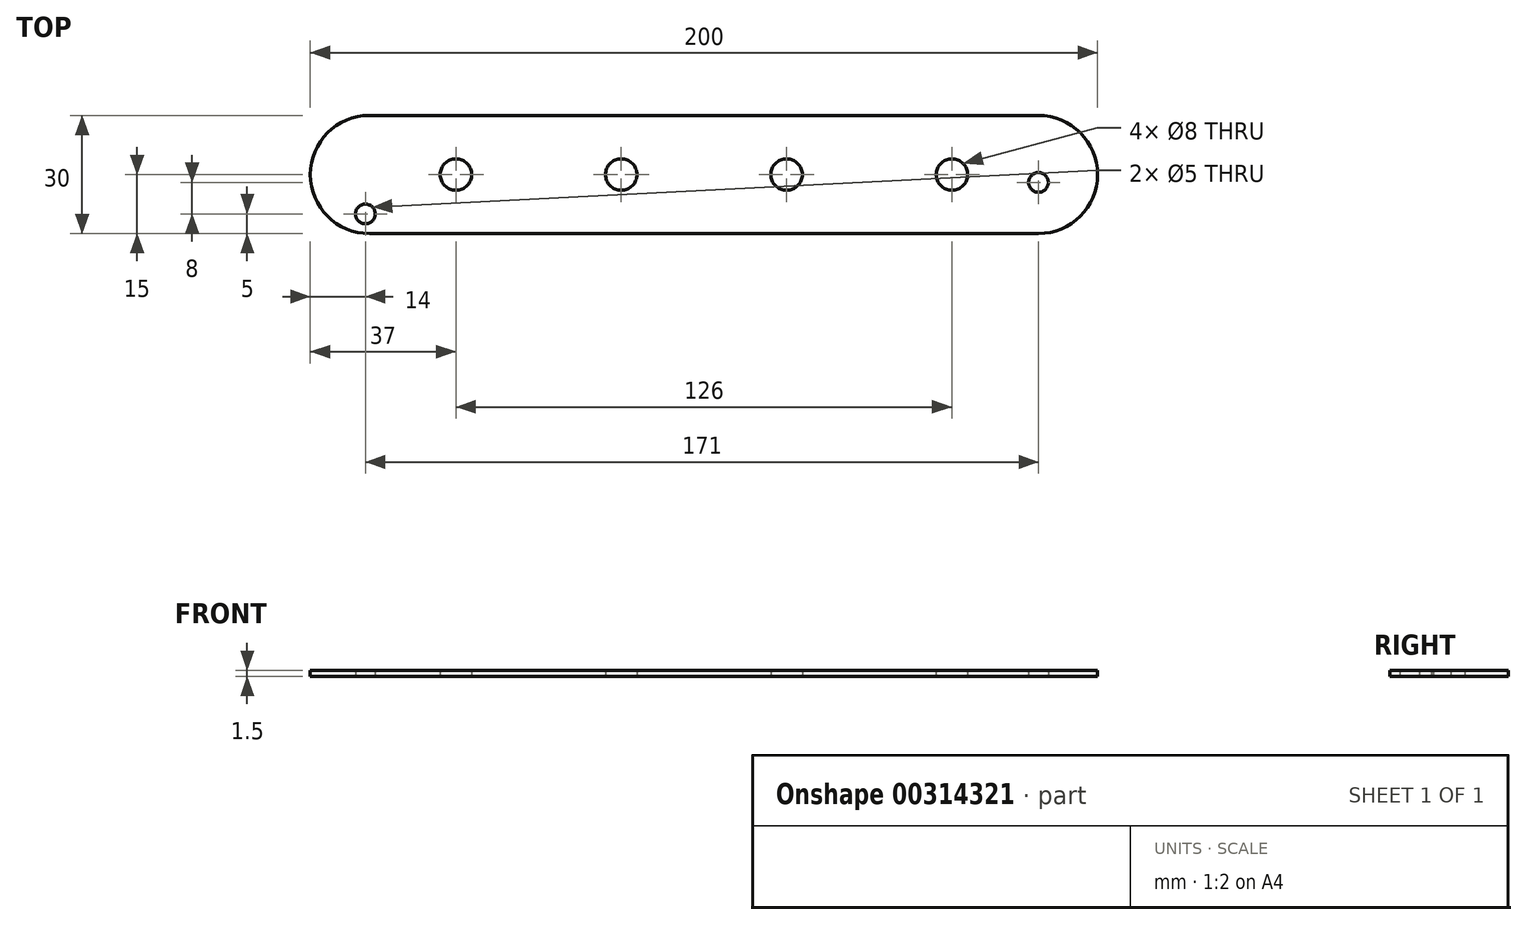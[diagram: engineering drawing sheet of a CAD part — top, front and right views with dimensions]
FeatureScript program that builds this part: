
annotation { "Feature Type Name" : "Feature", "Feature Type Description" : "" }
export const myFeature = defineFeature(function(context is Context, id is Id, definition is map)
    precondition{}
    {
        {
            var Q0;
            Q0=qCreatedBy(makeId("Top.planeOp"),FACE);
            var sketch = newSketch(context, id + "F0", { "sketchPlane" : qUnion([Q0])});
            skLineSegment(sketch, "E0.bottom", {"start": v(100, 15) * mm, "end": v(-100, 15) * mm});
            skLineSegment(sketch, "E0.top", {"start": v(100, -15) * mm, "end": v(-100, -15) * mm});
            skLineSegment(sketch, "E0.left", {"start": v(100, 15) * mm, "end": v(100, -15) * mm});
            skLineSegment(sketch, "E0.right", {"start": v(-100, 15) * mm, "end": v(-100, -15) * mm});
            skPoint(sketch, "E0.middle", {"position": v(0, 0) * mm});
            skCircle(sketch, "E1", {"center": v(21, 0) * mm, "radius": 4 * mm});
            skCircle(sketch, "E2", {"center": v(-21, 0) * mm, "radius": 4 * mm});
            skCircle(sketch, "E3", {"center": v(63, 0) * mm, "radius": 4 * mm});
            skCircle(sketch, "E4", {"center": v(-63, 0) * mm, "radius": 4 * mm});
            skCircle(sketch, "E5", {"center": v(-86, -10) * mm, "radius": 2.5 * mm});
            skCircle(sketch, "E6", {"center": v(85, -2) * mm, "radius": 2.5 * mm});
            skSolve(sketch);
        }
        {
            var Q0;
            Q0=makeQuery(id+"F0.imprint","IMPRINT",FACE,{"disambiguationData":[TD([[makeQuery(id+"F0.imprint","IMPRINT",EDGE,{"derivedFrom":sQuery(id+"F0.wireOp",EDGE,"E0.bottom")}),1.0]])]});
            extrude(context, id + "F1", {"entities" : qUnion([Q0]), "depth" : 1.5 * mm});
        }
        {
            var Q0;
            Q0=makeQuery(id+"F1.opExtrude","SWEPT_EDGE",EDGE,{"disambiguationData":[OSD([sQuery(id+"F0.wireOp",EDGE,"E0.top"),sQuery(id+"F0.wireOp",EDGE,"E0.right")])]});
            var Q1;
            Q1=makeQuery(id+"F1.opExtrude","SWEPT_EDGE",EDGE,{"disambiguationData":[OSD([sQuery(id+"F0.wireOp",EDGE,"E0.bottom"),sQuery(id+"F0.wireOp",EDGE,"E0.right")])]});
            var Q2;
            Q2=makeQuery(id+"F1.opExtrude","SWEPT_EDGE",EDGE,{"disambiguationData":[OSD([sQuery(id+"F0.wireOp",EDGE,"E0.top"),sQuery(id+"F0.wireOp",EDGE,"E0.left")])]});
            var Q3;
            Q3=makeQuery(id+"F1.opExtrude","SWEPT_EDGE",EDGE,{"disambiguationData":[OSD([sQuery(id+"F0.wireOp",EDGE,"E0.bottom"),sQuery(id+"F0.wireOp",EDGE,"E0.left")])]});
            fillet(context, id + "F2", {"entities" : qUnion([Q0, Q1, Q2, Q3]), "radius" : 15 * mm, "tangentPropagation" : true, "allowEdgeOverflow" : false});
        }
    });
